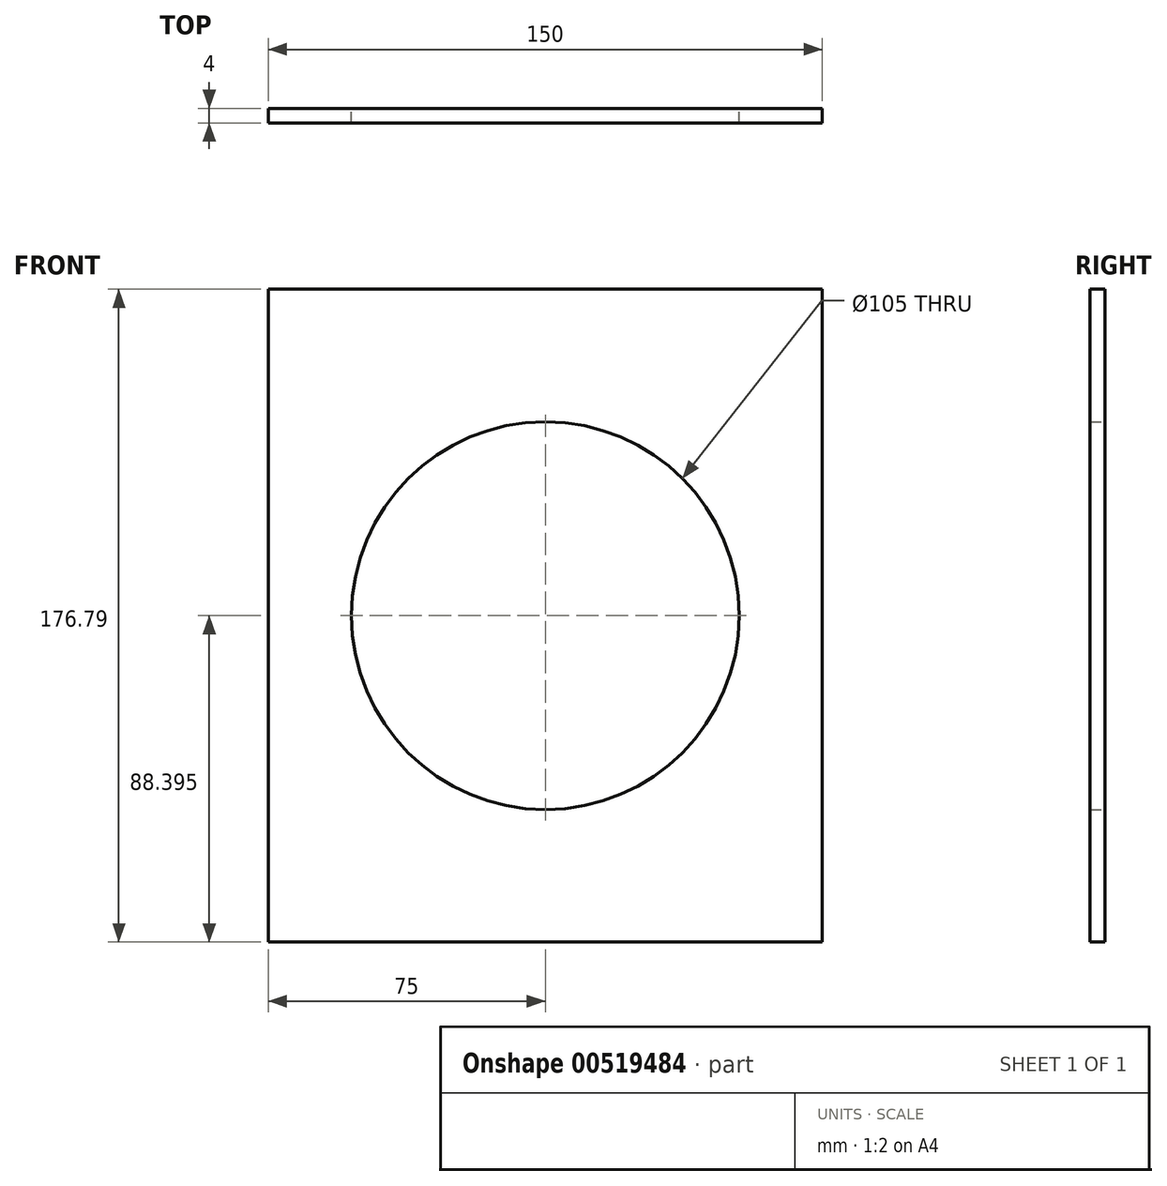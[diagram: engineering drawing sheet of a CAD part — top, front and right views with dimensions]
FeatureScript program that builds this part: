
annotation { "Feature Type Name" : "Feature", "Feature Type Description" : "" }
export const myFeature = defineFeature(function(context is Context, id is Id, definition is map)
    precondition{}
    {
        {
            var Q0;
            Q0=qCreatedBy(makeId("Front.planeOp"),FACE);
            var sketch = newSketch(context, id + "F0", { "sketchPlane" : qUnion([Q0])});
            skLineSegment(sketch, "E0.bottom", {"start": v(0, 0) * mm, "end": v(150, 0) * mm});
            skLineSegment(sketch, "E0.top", {"start": v(0, 176.79) * mm, "end": v(150, 176.79) * mm});
            skLineSegment(sketch, "E0.left", {"start": v(0, 0) * mm, "end": v(0, 176.79) * mm});
            skLineSegment(sketch, "E0.right", {"start": v(150, 0) * mm, "end": v(150, 176.8) * mm});
            skCircle(sketch, "E1", {"center": v(75, 88.4) * mm, "radius": 52.5 * mm});
            skPoint(sketch, "E1.centerSnap0", {"position": v(0, 88.4) * mm});
            skPoint(sketch, "E1.centerSnap1", {"position": v(75, 176.79) * mm});
            skSolve(sketch);
        }
        {
            var Q0;
            Q0=makeQuery(id+"F0.imprint","IMPRINT",FACE,{"disambiguationData":[TD([[makeQuery(id+"F0.imprint","IMPRINT",EDGE,{"derivedFrom":sQuery(id+"F0.wireOp",EDGE,"E0.bottom")}),1.0]])]});
            extrude(context, id + "F1", {"entities" : qUnion([Q0]), "depth" : 4 * mm, "offsetDistance" : 25 * mm});
        }
    });
